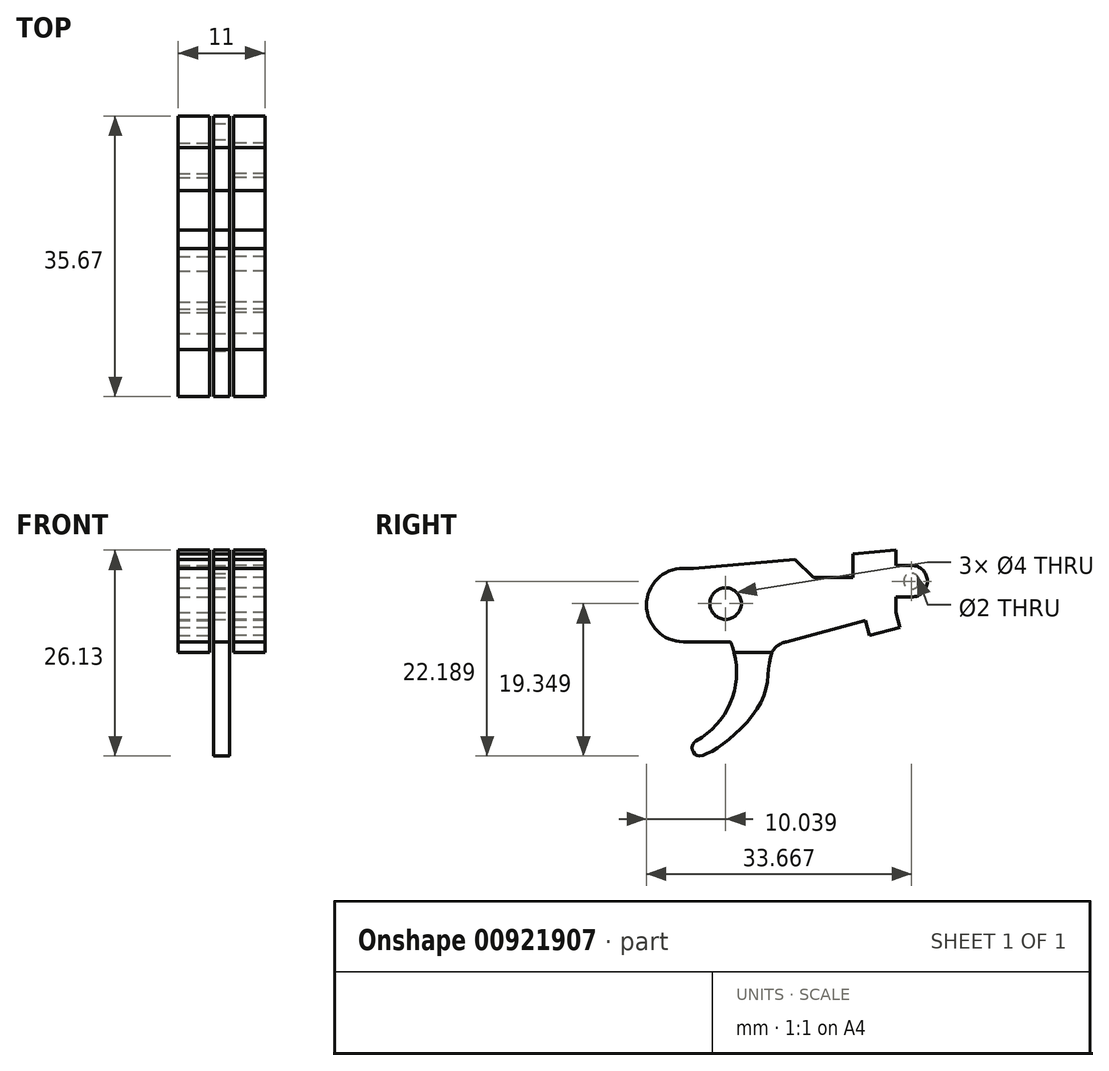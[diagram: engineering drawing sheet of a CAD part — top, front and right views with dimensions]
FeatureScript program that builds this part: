
annotation { "Feature Type Name" : "Feature", "Feature Type Description" : "" }
export const myFeature = defineFeature(function(context is Context, id is Id, definition is map)
    precondition{}
    {
        {
            var Q0;
            Q0=qCreatedBy(makeId("Right.planeOp"),FACE);
            var sketch = newSketch(context, id + "F0", { "sketchPlane" : qUnion([Q0])});
            skArc(sketch, "E0", {"start": v(69.9, -26.22) * mm, "mid": v(74.5, -20.75) * mm, "end": v(74.27, -13.62) * mm});
            skFitSpline(sketch, "E1", {"points": [v(69.02, -26.65) * mm, v(70.45, -28.1) * mm, v(78.54, -20.33) * mm, v(81.38, -13.62) * mm], "startDerivative": vector(8.58, -15.93) * mm, "endDerivative": vector(25.25, 5.8) * mm});
            skArc(sketch, "E2.filletArc", {"start": v(69.9, -26.22) * mm, "mid": v(69.42, -26.84) * mm, "end": v(69.54, -27.62) * mm});
            skLineSegment(sketch, "E3.bottom", {"start": v(48.56, -15) * mm, "end": v(84.3, -15) * mm});
            skLineSegment(sketch, "E3.top", {"start": v(54.02, -30) * mm, "end": v(77.1, -30) * mm});
            skPoint(sketch, "E4.visualSharp", {"position": v(54.02, -30) * mm});
            skLineSegment(sketch, "E5", {"start": v(90.2, -37.17) * mm, "end": v(102.71, -70.13) * mm});
            skLineSegment(sketch, "E6", {"start": v(105.52, -72.07) * mm, "end": v(129.1, -72.07) * mm});
            skLineSegment(sketch, "E7", {"start": v(131.9, -68) * mm, "end": v(116.08, -26.33) * mm});
            skPoint(sketch, "E8.visualSharp", {"position": v(103.45, -72.07) * mm});
            skArc(sketch, "E8.filletArc", {"start": v(102.71, -70.13) * mm, "mid": v(103.81, -71.54) * mm, "end": v(105.52, -72.07) * mm});
            skLineSegment(sketch, "E9", {"start": v(52.63, -32.01) * mm, "end": v(82.72, -32.01) * mm});
            skPoint(sketch, "E10.visualSharp", {"position": v(133.45, -72.07) * mm});
            skArc(sketch, "E10.filletArc", {"start": v(129.1, -72.07) * mm, "mid": v(131.57, -70.77) * mm, "end": v(131.9, -68) * mm});
            skPoint(sketch, "E11.visualSharp", {"position": v(88.23, -32.01) * mm});
            skArc(sketch, "E11.filletArc", {"start": v(90.2, -37.17) * mm, "mid": v(87.26, -33.43) * mm, "end": v(82.72, -32.01) * mm});
            skPoint(sketch, "E12.newPointB", {"position": v(87.47, -30) * mm});
            skLineSegment(sketch, "E13", {"start": v(114.08, 0) * mm, "end": v(114.97, -11.78) * mm});
            skLineSegment(sketch, "E14.bottom", {"start": v(68.26, -4.3) * mm, "end": v(69.58, -4.3) * mm});
            skLineSegment(sketch, "E14.right", {"start": v(95.27, -1.99) * mm, "end": v(95.27, -9.87) * mm});
            skLineSegment(sketch, "E15.trimOffspring", {"start": v(68.26, -13.62) * mm, "end": v(74.27, -13.62) * mm});
            skLineSegment(sketch, "E16", {"start": v(91.8, 0) * mm, "end": v(91.8, -2) * mm});
            skLineSegment(sketch, "E17", {"start": v(91.8, -2) * mm, "end": v(97.8, -1.46) * mm});
            skCircle(sketch, "E18", {"center": v(73.64, -8.77) * mm, "radius": 2 * mm});
            skLineSegment(sketch, "E19.0", {"start": v(69.58, -4.3) * mm, "end": v(82.45, -3.14) * mm});
            skLineSegment(sketch, "E20", {"start": v(89.8, -2.48) * mm, "end": v(89.8, -5.48) * mm});
            skLineSegment(sketch, "E21", {"start": v(89.8, -5.48) * mm, "end": v(84.8, -5.48) * mm});
            skLineSegment(sketch, "E22.trimOffspring", {"start": v(89.8, -2.48) * mm, "end": v(95.27, -1.99) * mm});
            skLineSegment(sketch, "E23", {"start": v(84.8, -5.48) * mm, "end": v(82.45, -3.14) * mm});
            skArc(sketch, "E24", {"start": v(68.26, -4.3) * mm, "mid": v(63.6, -8.96) * mm, "end": v(68.26, -13.62) * mm});
            skPoint(sketch, "E25.left.start.orphan", {"position": v(0, 0) * mm});
            skLineSegment(sketch, "E26", {"start": v(81.38, -13.62) * mm, "end": v(95.27, -9.87) * mm});
            skLineSegment(sketch, "E27.bottom", {"start": v(91.93, -12.85) * mm, "end": v(95.79, -11.8) * mm});
            skLineSegment(sketch, "E27.top", {"start": v(91.4, -10.91) * mm, "end": v(95.27, -9.87) * mm});
            skLineSegment(sketch, "E27.left", {"start": v(91.93, -12.85) * mm, "end": v(91.4, -10.91) * mm});
            skLineSegment(sketch, "E27.right", {"start": v(95.79, -11.8) * mm, "end": v(95.27, -9.87) * mm});
            skFitSpline(sketch, "E28", {"points": [v(116.08, -26.33) * mm, v(116.83, -20.27) * mm, v(119.18, -16.92) * mm, v(122.92, -14.6) * mm, v(128.1, -12.98) * mm], "startDerivative": vector(0.84, 23.64) * mm, "endDerivative": vector(20.66, 5.4) * mm});
            skArc(sketch, "E29", {"start": v(128.1, -12.98) * mm, "mid": v(128.98, -12.1) * mm, "end": v(128.1, -11.23) * mm});
            skLineSegment(sketch, "E30", {"start": v(128.1, -11.23) * mm, "end": v(114.97, -11.78) * mm});
            skLineSegment(sketch, "E31", {"start": v(-48.1, -15) * mm, "end": v(47.18, -17.05) * mm});
            skLineSegment(sketch, "E32", {"start": v(54.02, -30) * mm, "end": v(48.56, -15) * mm});
            skFitSpline(sketch, "E33.0", {"points": [v(64.62, -29.02) * mm, v(64.67, -29.12) * mm, v(64.78, -29.32) * mm, v(64.99, -29.73) * mm, v(65.27, -30.24) * mm, v(65.65, -30.79) * mm, v(66.05, -31.28) * mm, v(66.61, -31.82) * mm, v(67.36, -32.35) * mm, v(68.26, -32.79) * mm, v(69.22, -33.05) * mm, v(70.11, -33.14) * mm, v(70.9, -33.1) * mm, v(71.54, -33) * mm, v(72.27, -32.82) * mm, v(73.02, -32.55) * mm, v(73.81, -32.18) * mm, v(74.56, -31.77) * mm, v(75.3, -31.32) * mm, v(76.03, -30.82) * mm, v(77, -30.1) * mm, v(78.23, -29.07) * mm, v(79.66, -27.66) * mm, v(80.8, -26.33) * mm, v(81.64, -25.15) * mm, v(82.23, -24.22) * mm, v(82.68, -23.37) * mm, v(83, -22.66) * mm, v(83.19, -22.2) * mm, v(83.32, -21.81) * mm, v(83.44, -21.44) * mm, v(83.58, -20.98) * mm, v(83.7, -20.45) * mm, v(83.84, -19.78) * mm, v(83.95, -19.02) * mm, v(84.03, -18.23) * mm, v(84.09, -17.59) * mm, v(84.13, -17.19) * mm, v(84.15, -17) * mm, v(84.16, -16.91) * mm, v(84.17, -16.86) * mm, v(84.18, -16.84) * mm, v(84.18, -16.82) * mm, v(84.18, -16.82) * mm, v(84.18, -16.81) * mm, v(84.18, -16.81) * mm, v(84.18, -16.8) * mm, v(84.18, -16.81) * mm, v(84.18, -16.8) * mm, v(84.19, -16.8) * mm, v(84.2, -16.77) * mm, v(84.2, -16.75) * mm, v(84.2, -16.7) * mm, v(84.21, -16.67) * mm, v(84.22, -16.65) * mm]});
            skLineSegment(sketch, "E34", {"start": v(83.99, -18.66) * mm, "end": v(84.3, -15) * mm});
            skLineSegment(sketch, "E35.0", {"start": v(52.63, -32.01) * mm, "end": v(47.18, -17.05) * mm});
            skLineSegment(sketch, "E36.0", {"start": v(97.8, 0) * mm, "end": v(97.8, -1.46) * mm});
            skLineSegment(sketch, "E37", {"start": v(97.8, 0) * mm, "end": v(97.8, 2) * mm});
            skLineSegment(sketch, "E38", {"start": v(97.8, 2) * mm, "end": v(77.8, 2) * mm});
            skLineSegment(sketch, "E39", {"start": v(77.8, 2) * mm, "end": v(77.8, 6) * mm});
            skLineSegment(sketch, "E40", {"start": v(77.8, 6) * mm, "end": v(95.27, 10.4) * mm});
            skLineSegment(sketch, "E41", {"start": v(95.27, 10.4) * mm, "end": v(109.64, 10.4) * mm});
            skLineSegment(sketch, "E42", {"start": v(109.64, 10.4) * mm, "end": v(114.08, 0) * mm});
            skLineSegment(sketch, "E43", {"start": v(91.8, 0) * mm, "end": v(-48.1, 0) * mm});
            skLineSegment(sketch, "E44", {"start": v(-48.1, 0) * mm, "end": v(-48.1, -15) * mm});
            skLineSegment(sketch, "E45.0", {"start": v(95.27, -7.93) * mm, "end": v(97.27, -7.93) * mm});
            skLineSegment(sketch, "E46.0", {"start": v(95.27, -3.93) * mm, "end": v(97.27, -3.93) * mm});
            skArc(sketch, "E47", {"start": v(97.27, -7.93) * mm, "mid": v(99.27, -5.93) * mm, "end": v(97.27, -3.93) * mm});
            skCircle(sketch, "E48", {"center": v(97.27, -5.93) * mm, "radius": 1 * mm});
            skSolve(sketch);
        }
        {
            var Q0;
            Q0=makeQuery(id+"F0.imprint","IMPRINT",FACE,{"disambiguationData":[TD([[makeQuery(id+"F0.imprint","IMPRINT",EDGE,{"derivedFrom":sQuery(id+"F0.wireOp",EDGE,"E14.bottom")}),-1.0]])]});
            var Q1;
            {var subQ0=sQuery(id+"F0.wireOp",EDGE,"E15.trimOffspring");var subQ1=sQuery(id+"F0.wireOp",EDGE,"E0");var subQ2=makeQuery(id+"F0.imprint","INTERSECT",VERTEX,{"derivedFrom":[subQ1,subQ0]});Q1=makeQuery(id+"F0.imprint","IMPRINT",FACE,{"disambiguationData":[TD([[makeQuery(id+"F0.imprint","IMPRINT",EDGE,{"disambiguationData":[TD([[subQ2,1.0]])],"derivedFrom":subQ1}),-1.0]])]});}
            var Q2;
            {var subQ0=sQuery(id+"F0.wireOp",EDGE,"E2.filletArc");Q2=makeQuery(id+"F0.imprint","IMPRINT",FACE,{"disambiguationData":[TD([[makeQuery(id+"F0.imprint","IMPRINT",EDGE,{"derivedFrom":subQ0}),1.0]])]});}
            var Q3;
            {var subQ0=sQuery(id+"F0.wireOp",EDGE,"E45.0");Q3=makeQuery(id+"F0.imprint","IMPRINT",FACE,{"disambiguationData":[TD([[makeQuery(id+"F0.imprint","IMPRINT",EDGE,{"derivedFrom":subQ0}),1.0]])]});}
            extrude(context, id + "F1", {"entities" : qUnion([Q0, Q1, Q2, Q3]), "oppositeDirection" : true, "depth" : 2.5 * mm, "offsetDistance" : 25 * mm, "hasSecondDirection" : true, "secondDirectionOppositeDirection" : true, "secondDirectionDepth" : .5 * mm});
        }
        {
            var Q0;
            Q0=makeQuery(id+"F0.imprint","IMPRINT",FACE,{"disambiguationData":[TD([[makeQuery(id+"F0.imprint","IMPRINT",EDGE,{"derivedFrom":sQuery(id+"F0.wireOp",EDGE,"E25.bottom")}),-1.0]])]});
            var Q1;
            {var subQ0=sQuery(id+"F0.wireOp",EDGE,"E15.trimOffspring");var subQ1=sQuery(id+"F0.wireOp",EDGE,"E0");var subQ2=makeQuery(id+"F0.imprint","INTERSECT",VERTEX,{"derivedFrom":[subQ1,subQ0]});Q1=makeQuery(id+"F0.imprint","IMPRINT",FACE,{"disambiguationData":[TD([[makeQuery(id+"F0.imprint","IMPRINT",EDGE,{"disambiguationData":[TD([[subQ2,1.0]])],"derivedFrom":subQ1}),-1.0]])]});}
            var Q2;
            Q2=makeQuery(id+"F0.imprint","IMPRINT",FACE,{"disambiguationData":[TD([[makeQuery(id+"F0.imprint","IMPRINT",EDGE,{"derivedFrom":sQuery(id+"F0.wireOp",EDGE,"E14.bottom")}),-1.0]])]});
            var Q3;
            Q3=makeQuery(id+"F0.imprint","IMPRINT",FACE,{"disambiguationData":[TD([[makeQuery(id+"F0.imprint","IMPRINT",EDGE,{"derivedFrom":sQuery(id+"F0.wireOp",EDGE,"YsGSTseL-7c39-2jtd-xzSD-fyieAOXsv8hQ")}),1.0]])]});
            var Q4;
            Q4=makeQuery(id+"F0.imprint","IMPRINT",FACE,{"disambiguationData":[TD([[makeQuery(id+"F0.imprint","IMPRINT",EDGE,{"derivedFrom":sQuery(id+"F0.wireOp",EDGE,"E3.top")}),-1.0]])]});
            var Q5;
            {var subQ0=sQuery(id+"F0.wireOp",EDGE,"E45.0");Q5=makeQuery(id+"F0.imprint","IMPRINT",FACE,{"disambiguationData":[TD([[makeQuery(id+"F0.imprint","IMPRINT",EDGE,{"derivedFrom":subQ0}),1.0]])]});}
            var Q6;
            Q6=makeQuery(id+"F0.imprint","IMPRINT",FACE,{"disambiguationData":[TD([[makeQuery(id+"F0.imprint","IMPRINT",EDGE,{"derivedFrom":sQuery(id+"F0.wireOp",EDGE,"E48")}),1.0]])]});
            var Q7;
            Q7=makeQuery(id+"F0.imprint","IMPRINT",FACE,{"disambiguationData":[TD([[makeQuery(id+"F0.imprint","IMPRINT",EDGE,{"derivedFrom":sQuery(id+"F0.wireOp",EDGE,"E27.bottom")}),1.0]])]});
            extrude(context, id + "F2", {"entities" : qUnion([Q0, Q1, Q2, Q3, Q4, Q5, Q6, Q7]), "depth" : 4 * mm, "offsetDistance" : 25 * mm, "hasSecondDirection" : true, "secondDirectionOppositeDirection" : false, "secondDirectionDepth" : 0 * mm});
        }
        {
            var Q0;
            Q0=qCreatedBy(makeId("Right.planeOp"),FACE);
            cPlane(context, id + "F3", {"entities" : qUnion([Q0]), "cplaneType" : CPlaneType.OFFSET, "offset" : 1.5 * mm, "oppositeDirection" : true, "width" : 150 * mm, "height" : 150 * mm});
        }
        {
            var Q0;
            Q0=makeQuery(id+"F2.opExtrude","SWEPT_BODY",BODY,{"disambiguationData":[OSD([sQuery(id+"F0.wireOp",EDGE,"E25.bottom"),sQuery(id+"F0.wireOp",EDGE,"E25.top"),sQuery(id+"F0.wireOp",EDGE,"E25.left"),sQuery(id+"F0.wireOp",EDGE,"E3.bottom"),sQuery(id+"F0.wireOp",EDGE,"E3.top"),sQuery(id+"F0.wireOp",EDGE,"E4.filletArc"),sQuery(id+"F0.wireOp",EDGE,"56a3f3f5-f5d7-4775-ad63-b447ffa166db.filletArc"),sQuery(id+"F0.wireOp",EDGE,"E5"),sQuery(id+"F0.wireOp",EDGE,"E6"),sQuery(id+"F0.wireOp",EDGE,"E7"),sQuery(id+"F0.wireOp",EDGE,"E8.filletArc"),sQuery(id+"F0.wireOp",EDGE,"f3d2d942-5989-418b-ae13-af2c3b13bb26.0"),sQuery(id+"F0.wireOp",EDGE,"9f5465d0-8d63-4763-b605-d24600be065e.0"),sQuery(id+"F0.wireOp",EDGE,"E9"),sQuery(id+"F0.wireOp",EDGE,"83427892-dbcb-4f8f-812b-28bc47008b19"),sQuery(id+"F0.wireOp",EDGE,"E10.filletArc"),sQuery(id+"F0.wireOp",EDGE,"E11.filletArc"),sQuery(id+"F0.wireOp",EDGE,"1a0358dd-2d95-416f-8ec6-dd23ccaf9022"),sQuery(id+"F0.wireOp",EDGE,"E12.filletArc"),sQuery(id+"F0.wireOp",EDGE,"pYktnrQp-GeeN-XTcM-nB2k-1LKm4CGNClLe"),sQuery(id+"F0.wireOp",EDGE,"E13"),sQuery(id+"F0.wireOp",EDGE,"E14.top"),sQuery(id+"F0.wireOp",EDGE,"XYrIvgm7-XzCV-vxwV-3k3z-0Dzyygqc0baX"),sQuery(id+"F0.wireOp",EDGE,"E16"),sQuery(id+"F0.wireOp",EDGE,"E17"),sQuery(id+"F0.wireOp",EDGE,"E18"),sQuery(id+"F0.wireOp",EDGE,"YsGSTseL-7c39-2jtd-xzSD-fyieAOXsv8hQ")])]});
            var Q1;
            Q1=qCreatedBy(id+"F3.planeOp",FACE);
            mirror(context, id + "F4", {"entities" : qUnion([Q0]), "mirrorPlane" : qUnion([Q1])});
        }
    });
